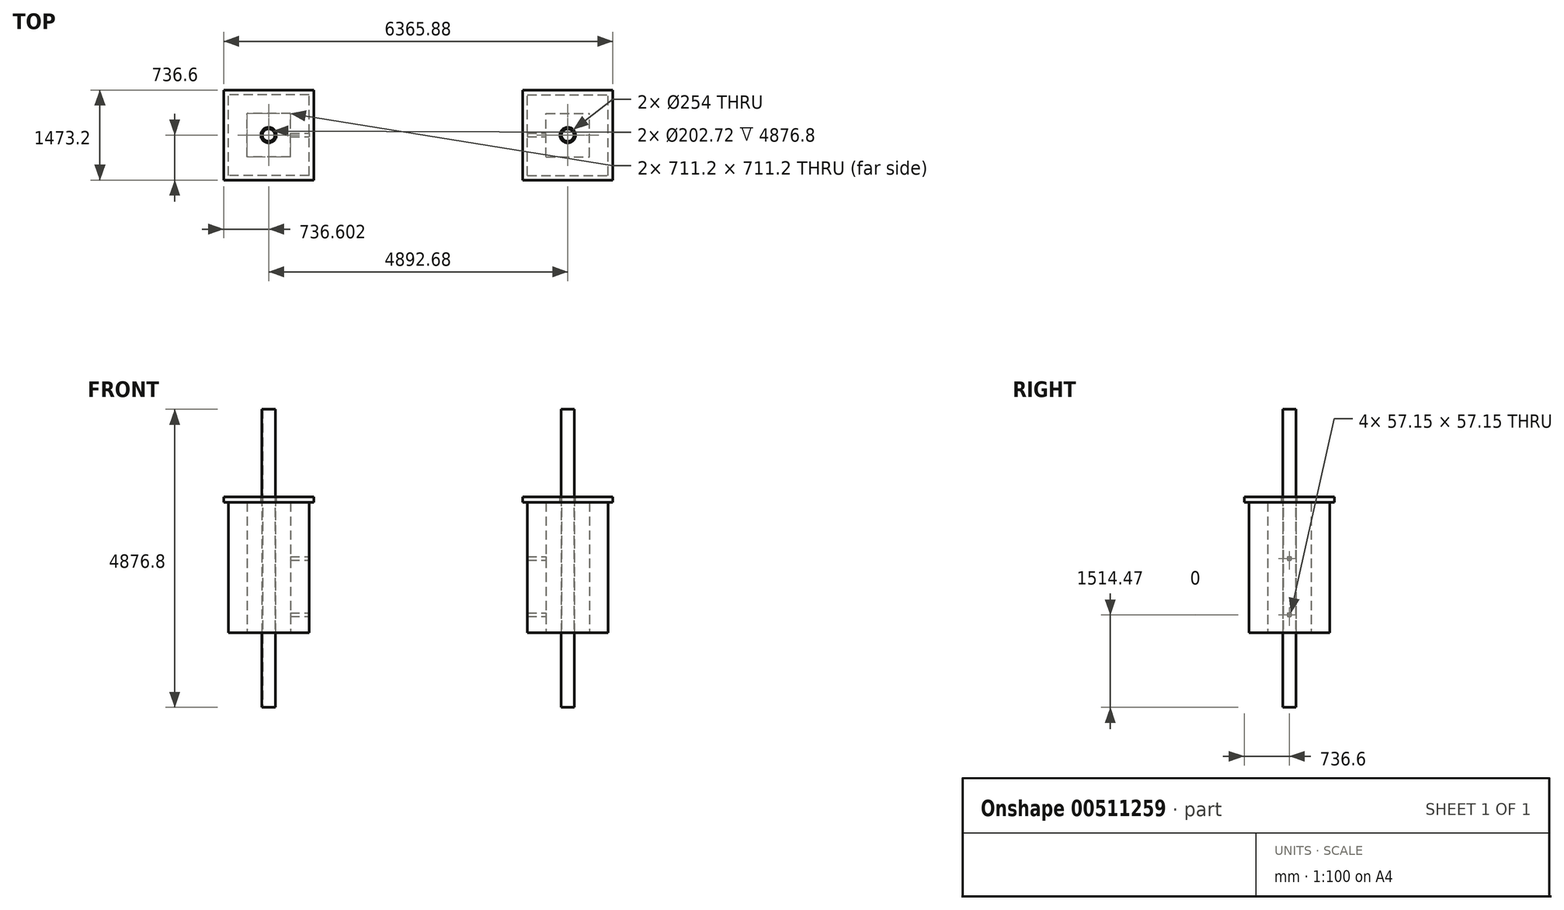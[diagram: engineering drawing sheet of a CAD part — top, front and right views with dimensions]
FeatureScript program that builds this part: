
annotation { "Feature Type Name" : "Feature", "Feature Type Description" : "" }
export const myFeature = defineFeature(function(context is Context, id is Id, definition is map)
    precondition{}
    {
        {
            var Q0;
            Q0=qCreatedBy(makeId("Top.planeOp"),FACE);
            var sketch = newSketch(context, id + "F0", { "sketchPlane" : qUnion([Q0])});
            skLineSegment(sketch, "E0.bottom", {"start": v(-1785.94, -660.4) * mm, "end": v(-3106.74, -660.4) * mm});
            skLineSegment(sketch, "E0.top", {"start": v(-1785.94, 660.4) * mm, "end": v(-3106.74, 660.4) * mm});
            skLineSegment(sketch, "E0.left", {"start": v(-1785.94, -660.4) * mm, "end": v(-1785.94, 660.4) * mm});
            skLineSegment(sketch, "E0.right", {"start": v(-3106.74, -660.4) * mm, "end": v(-3106.74, 660.4) * mm});
            skPoint(sketch, "E0.middle", {"position": v(-2446.34, 0) * mm});
            skLineSegment(sketch, "E1", {"start": v(-1785.94, 0) * mm, "end": v(1785.94, 0) * mm, "construction": true});
            skPoint(sketch, "E2", {"position": v(0, 0) * mm});
            skLineSegment(sketch, "E3", {"start": v(0, 0) * mm, "end": v(0, 721.5) * mm, "construction": true});
            skPoint(sketch, "E4.MirrorP", {"position": v(2446.34, 0) * mm});
            skLineSegment(sketch, "E5.MirrorCS", {"start": v(1785.94, -660.4) * mm, "end": v(3106.74, -660.4) * mm});
            skLineSegment(sketch, "E6.MirrorCS", {"start": v(1785.94, 660.4) * mm, "end": v(3106.74, 660.4) * mm});
            skLineSegment(sketch, "E7.MirrorCS", {"start": v(3106.74, -660.4) * mm, "end": v(3106.74, 660.4) * mm});
            skLineSegment(sketch, "E8.MirrorCS", {"start": v(1785.94, -660.4) * mm, "end": v(1785.94, 660.4) * mm});
            skLineSegment(sketch, "E9.0", {"start": v(-2090.74, 355.6) * mm, "end": v(-2801.94, 355.6) * mm});
            skLineSegment(sketch, "E9.1", {"start": v(-2090.74, -355.6) * mm, "end": v(-2090.74, 355.6) * mm});
            skLineSegment(sketch, "E9.2", {"start": v(-2090.74, -355.6) * mm, "end": v(-2801.94, -355.6) * mm});
            skLineSegment(sketch, "E9.3", {"start": v(-2801.94, -355.6) * mm, "end": v(-2801.94, 355.6) * mm});
            skLineSegment(sketch, "E10.MirrorCS", {"start": v(2801.94, -355.6) * mm, "end": v(2801.94, 355.6) * mm});
            skLineSegment(sketch, "E11.MirrorCS", {"start": v(2090.74, 355.6) * mm, "end": v(2801.94, 355.6) * mm});
            skLineSegment(sketch, "E12.MirrorCS", {"start": v(2090.74, -355.6) * mm, "end": v(2801.94, -355.6) * mm});
            skLineSegment(sketch, "E13.MirrorCS", {"start": v(2090.74, -355.6) * mm, "end": v(2090.74, 355.6) * mm});
            skCircle(sketch, "E14", {"center": v(-2446.34, 0) * mm, "radius": 109.54 * mm, "construction": true});
            skCircle(sketch, "E15", {"center": v(2446.34, 0) * mm, "radius": 109.54 * mm, "construction": true});
            skPoint(sketch, "E16", {"position": v(-2336.8, 0) * mm});
            skPoint(sketch, "E17", {"position": v(2336.8, 0) * mm});
            skPoint(sketch, "E17.positionSnap0", {"position": v(2801.94, 0) * mm});
            skSolve(sketch);
        }
        {
            var Q0;
            Q0=qSketchRegion(id+"F0",true);
            extrude(context, id + "F1", {"entities" : qUnion([Q0]), "depth" : 2133.6 * mm});
        }
        {
            var Q0;
            Q0=makeQuery(id+"F1.opExtrude","CAP_FACE",FACE,{"disambiguationData":[OSD([sQuery(id+"F0.wireOp",EDGE,"E0.bottom"),sQuery(id+"F0.wireOp",EDGE,"E0.top"),sQuery(id+"F0.wireOp",EDGE,"E0.left"),sQuery(id+"F0.wireOp",EDGE,"E0.right")])],"isStart":false});
            var sketch = newSketch(context, id + "F2", { "sketchPlane" : qUnion([Q0])});
            skLineSegment(sketch, "E18", {"start": v(-2446.34, -660.4) * mm, "end": v(-2446.34, 660.4) * mm, "construction": true});
            skLineSegment(sketch, "E19.bottom", {"start": v(-1709.74, -736.6) * mm, "end": v(-3182.94, -736.6) * mm});
            skLineSegment(sketch, "E19.top", {"start": v(-1709.74, 736.6) * mm, "end": v(-3182.94, 736.6) * mm});
            skLineSegment(sketch, "E19.left", {"start": v(-1709.74, -736.6) * mm, "end": v(-1709.74, 736.6) * mm});
            skLineSegment(sketch, "E19.right", {"start": v(-3182.94, -736.6) * mm, "end": v(-3182.94, 736.6) * mm});
            skPoint(sketch, "E19.middle", {"position": v(-2446.34, 0) * mm});
            skSolve(sketch);
        }
        {
            var Q0;
            Q0=qSketchRegion(id+"F2",true);
            extrude(context, id + "F3", {"entities" : qUnion([Q0]), "depth" : 88.9 * mm});
        }
        {
            var Q0;
            Q0=makeQuery(id+"F3.opExtrude","CAP_FACE",FACE,{"disambiguationData":[OSD([sQuery(id+"F2.wireOp",EDGE,"E19.bottom"),sQuery(id+"F2.wireOp",EDGE,"E19.top"),sQuery(id+"F2.wireOp",EDGE,"E19.left"),sQuery(id+"F2.wireOp",EDGE,"E19.right")])],"isStart":false});
            var sketch = newSketch(context, id + "F4", { "sketchPlane" : qUnion([Q0])});
            skLineSegment(sketch, "E20", {"start": v(-2446.34, 736.6) * mm, "end": v(-2446.34, -736.6) * mm, "construction": true});
            skCircle(sketch, "E21", {"center": v(-2446.34, 0) * mm, "radius": 127 * mm});
            skSolve(sketch);
        }
        {
            var Q0;
            Q0 = qSketchRegion(id + "F4", true);
            extrude(context, id + "F5", {"entities" : qUnion([Q0]), "operationType" : NewBodyOperationType.REMOVE, "endBound" : BoundingType.UP_TO_NEXT, "oppositeDirection" : true, "depth" : 25.4 * mm});
        }
        {
            var Q0;
            Q0=makeQuery(id+"F3.opExtrude","SWEPT_BODY",BODY,{"disambiguationData":[OSD([sQuery(id+"F2.wireOp",EDGE,"E19.bottom"),sQuery(id+"F2.wireOp",EDGE,"E19.top"),sQuery(id+"F2.wireOp",EDGE,"E19.left"),sQuery(id+"F2.wireOp",EDGE,"E19.right")])]});
            var Q1;
            Q1=qCreatedBy(makeId("Right.planeOp"),FACE);
            mirror(context, id + "F6", {"entities" : qUnion([Q0]), "mirrorPlane" : qUnion([Q1])});
        }
        {
            var Q0;
            Q0=qCreatedBy(makeId("Right.planeOp"),FACE);
            var sketch = newSketch(context, id + "F7", { "sketchPlane" : qUnion([Q0])});
            skLineSegment(sketch, "E22.bottom", {"start": v(-28.57, 323.85) * mm, "end": v(28.57, 323.85) * mm});
            skLineSegment(sketch, "E22.top", {"start": v(-28.57, 266.7) * mm, "end": v(28.57, 266.7) * mm});
            skLineSegment(sketch, "E22.left", {"start": v(-28.57, 323.85) * mm, "end": v(-28.57, 266.7) * mm});
            skLineSegment(sketch, "E22.right", {"start": v(28.58, 323.85) * mm, "end": v(28.58, 266.7) * mm});
            skLineSegment(sketch, "E23.bottom", {"start": v(-28.58, 1244.6) * mm, "end": v(28.57, 1244.6) * mm});
            skLineSegment(sketch, "E23.top", {"start": v(-28.57, 1187.45) * mm, "end": v(28.57, 1187.45) * mm});
            skLineSegment(sketch, "E23.left", {"start": v(-28.58, 1244.6) * mm, "end": v(-28.58, 1187.45) * mm});
            skLineSegment(sketch, "E23.right", {"start": v(28.57, 1244.6) * mm, "end": v(28.57, 1187.45) * mm});
            skPoint(sketch, "E24", {"position": v(0, 266.7) * mm});
            skSolve(sketch);
        }
        {
            var Q0;
            Q0 = qSketchRegion(id + "F7", true);
            var Q1;
            Q1=makeQuery(id+"F1.opExtrude","SWEPT_FACE",FACE,{"disambiguationData":[OSD([sQuery(id+"F0.wireOp",EDGE,"E9.1")])]});
            var Q2;
            Q2=makeQuery(id+"F1.opExtrude","SWEPT_FACE",FACE,{"disambiguationData":[OSD([sQuery(id+"F0.wireOp",EDGE,"E13.MirrorCS")])]});
            extrude(context, id + "F8", {"entities" : qUnion([Q0]), "operationType" : NewBodyOperationType.REMOVE, "endBound" : BoundingType.UP_TO_SURFACE, "oppositeDirection" : true, "endBoundEntityFace" : qUnion([Q1]), "depth" : 152.4 * mm, "hasSecondDirection" : true, "secondDirectionBound" : SecondDirectionBoundingType.UP_TO_SURFACE, "secondDirectionOppositeDirection" : false, "secondDirectionBoundEntityFace" : qUnion([Q2]), "secondDirectionDepth" : 25.4 * mm});
        }
        {
            var Q0;
            Q0=qCreatedBy(makeId("Top.planeOp"),FACE);
            var sketch = newSketch(context, id + "F9", { "sketchPlane" : qUnion([Q0])});
            skCircle(sketch, "E25.0", {"center": v(-2446.34, 0) * mm, "radius": 127 * mm, "construction": true});
            skCircle(sketch, "E26", {"center": v(-2446.34, 0) * mm, "radius": 109.54 * mm});
            skCircle(sketch, "E27.0", {"center": v(-2446.34, 0) * mm, "radius": 101.36 * mm});
            skSolve(sketch);
        }
        {
            var Q0;
            Q0 = qSketchRegion(id + "F9", true);
            extrude(context, id + "F10", {"entities" : qUnion([Q0]), "depth" : 3657.6 * mm, "hasSecondDirection" : true, "secondDirectionOppositeDirection" : true, "secondDirectionDepth" : 1219.2 * mm});
        }
        {
            var Q0;
            Q0=makeQuery(id+"F10.opExtrude","SWEPT_BODY",BODY,{"disambiguationData":[OSD([sQuery(id+"F9.wireOp",EDGE,"E26"),sQuery(id+"F9.wireOp",EDGE,"E27.0")])]});
            var Q1;
            Q1=qCreatedBy(makeId("Right.planeOp"),FACE);
            mirror(context, id + "F11", {"entities" : qUnion([Q0]), "mirrorPlane" : qUnion([Q1])});
        }
    });
